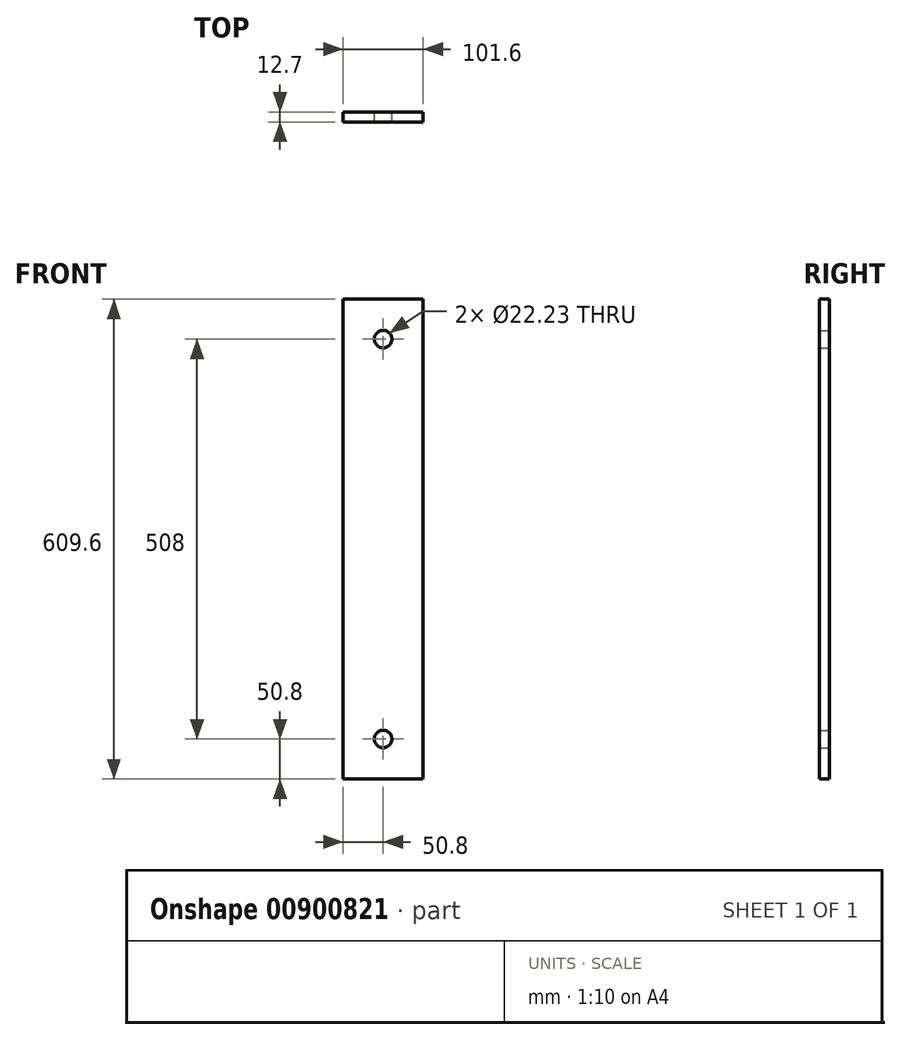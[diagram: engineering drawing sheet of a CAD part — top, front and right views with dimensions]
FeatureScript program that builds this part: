
annotation { "Feature Type Name" : "Feature", "Feature Type Description" : "" }
export const myFeature = defineFeature(function(context is Context, id is Id, definition is map)
    precondition{}
    {
        {
            var Q0;
            Q0=qCreatedBy(makeId("Front.planeOp"),FACE);
            var sketch = newSketch(context, id + "F0", { "sketchPlane" : qUnion([Q0])});
            skLineSegment(sketch, "E0.bottom", {"start": v(50.8, -304.8) * mm, "end": v(-50.8, -304.8) * mm});
            skLineSegment(sketch, "E0.top", {"start": v(50.8, 304.8) * mm, "end": v(-50.8, 304.8) * mm});
            skLineSegment(sketch, "E0.left", {"start": v(50.8, -304.8) * mm, "end": v(50.8, 304.8) * mm});
            skLineSegment(sketch, "E0.right", {"start": v(-50.8, -304.8) * mm, "end": v(-50.8, 304.8) * mm});
            skPoint(sketch, "E0.middle", {"position": v(0, 0) * mm});
            skCircle(sketch, "E1", {"center": v(0, 254) * mm, "radius": 11.11 * mm});
            skPoint(sketch, "E1.centerSnap0", {"position": v(0, 304.8) * mm});
            skCircle(sketch, "E2.MirrorC", {"center": v(0, -254) * mm, "radius": 11.11 * mm});
            skSolve(sketch);
        }
        {
            var Q0;
            Q0 = qSketchRegion(id + "F0", true);
            extrude(context, id + "F1", {"entities" : qUnion([Q0]), "depth" : 12.7 * mm, "offsetDistance" : 25.4 * mm});
        }
    });
